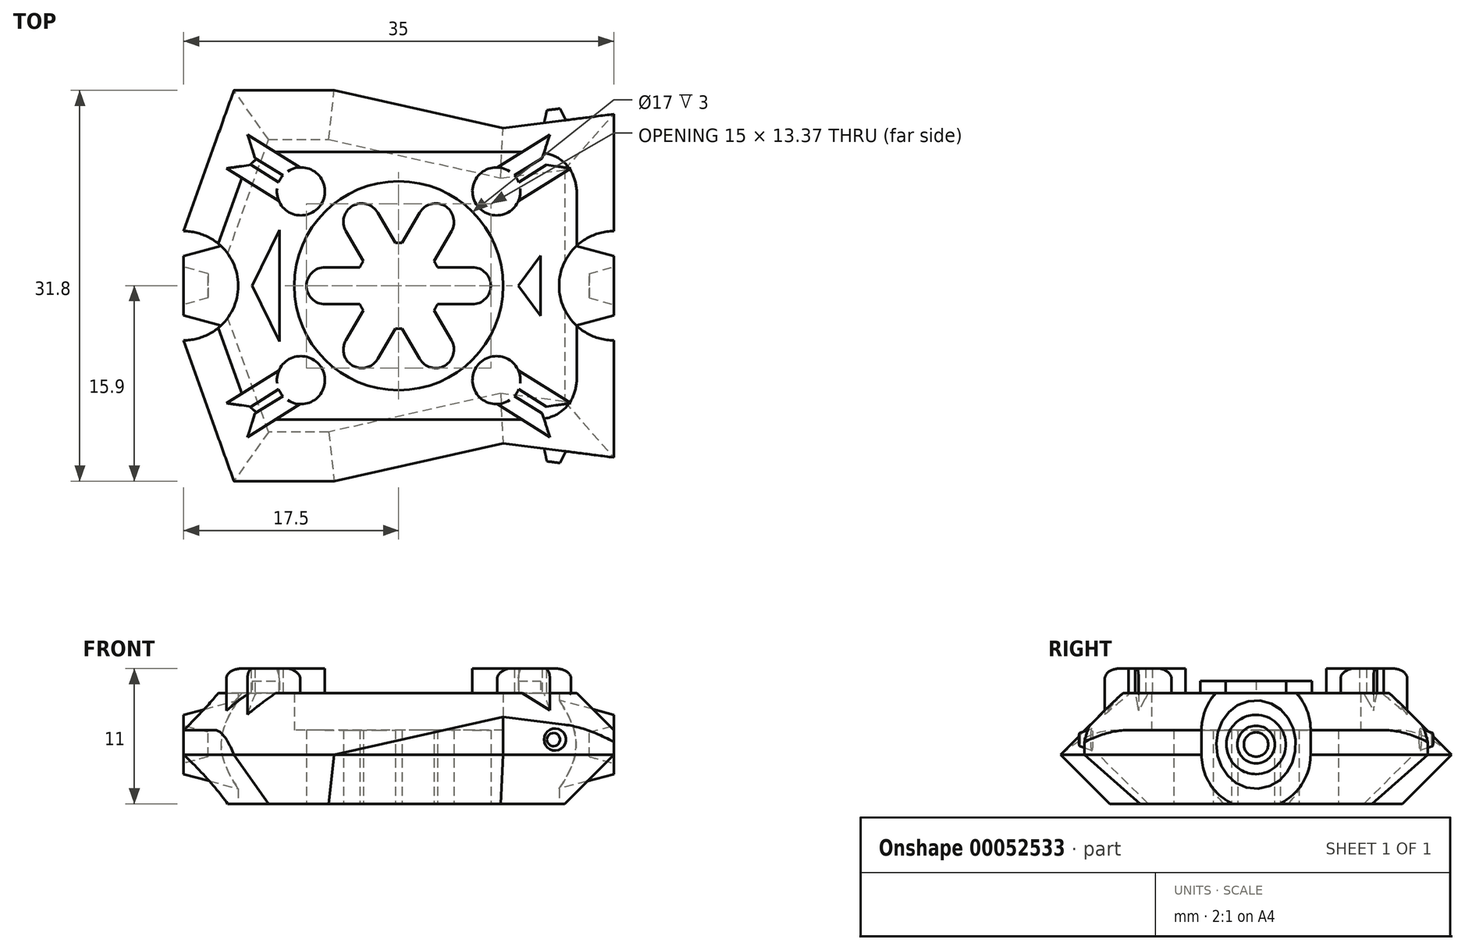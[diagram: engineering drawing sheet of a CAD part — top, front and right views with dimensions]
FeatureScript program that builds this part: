
annotation { "Feature Type Name" : "Feature", "Feature Type Description" : "" }
export const myFeature = defineFeature(function(context is Context, id is Id, definition is map)
    precondition{}
    {
        {
            var Q0;
            Q0=qCreatedBy(makeId("Top.planeOp"),FACE);
            var sketch = newSketch(context, id + "F0", { "sketchPlane" : qUnion([Q0])});
            skCircle(sketch, "E0", {"center": v(0, 0) * mm, "radius": 8.5 * mm});
            skCircle(sketch, "E1", {"center": v(0, 0) * mm, "radius": 3.5 * mm});
            skArc(sketch, "E2", {"start": v(6, -1.5) * mm, "mid": v(7.5, 0) * mm, "end": v(6, 1.5) * mm});
            skLineSegment(sketch, "E3", {"start": v(6, 1.5) * mm, "end": v(0, 1.5) * mm});
            skLineSegment(sketch, "E4", {"start": v(6, -1.5) * mm, "end": v(0, -1.5) * mm});
            skLineSegment(sketch, "E5.1.0", {"start": v(1.7, 5.95) * mm, "end": v(-1.3, 0.75) * mm});
            skLineSegment(sketch, "E5.1.1", {"start": v(4.3, 4.45) * mm, "end": v(1.3, -0.75) * mm});
            skArc(sketch, "E5.1.2", {"start": v(4.3, 4.45) * mm, "mid": v(3.75, 6.5) * mm, "end": v(1.7, 5.95) * mm});
            skLineSegment(sketch, "E5.2.0", {"start": v(-4.3, 4.45) * mm, "end": v(-1.3, -0.75) * mm});
            skLineSegment(sketch, "E5.2.1", {"start": v(-1.7, 5.95) * mm, "end": v(1.3, 0.75) * mm});
            skArc(sketch, "E5.2.2", {"start": v(-1.7, 5.95) * mm, "mid": v(-3.75, 6.5) * mm, "end": v(-4.3, 4.45) * mm});
            skLineSegment(sketch, "E5.3.0", {"start": v(-6, -1.5) * mm, "end": v(0, -1.5) * mm});
            skLineSegment(sketch, "E5.3.1", {"start": v(-6, 1.5) * mm, "end": v(0, 1.5) * mm});
            skArc(sketch, "E5.3.2", {"start": v(-6, 1.5) * mm, "mid": v(-7.5, 0) * mm, "end": v(-6, -1.5) * mm});
            skLineSegment(sketch, "E5.4.0", {"start": v(-1.7, -5.95) * mm, "end": v(1.3, -0.75) * mm});
            skLineSegment(sketch, "E5.4.1", {"start": v(-4.3, -4.45) * mm, "end": v(-1.3, 0.75) * mm});
            skArc(sketch, "E5.4.2", {"start": v(-4.3, -4.45) * mm, "mid": v(-3.75, -6.5) * mm, "end": v(-1.7, -5.95) * mm});
            skLineSegment(sketch, "E5.5.0", {"start": v(4.3, -4.45) * mm, "end": v(1.3, 0.75) * mm});
            skLineSegment(sketch, "E5.5.1", {"start": v(1.7, -5.95) * mm, "end": v(-1.3, -0.75) * mm});
            skArc(sketch, "E5.5.2", {"start": v(1.7, -5.95) * mm, "mid": v(3.75, -6.5) * mm, "end": v(4.3, -4.45) * mm});
            skSolve(sketch);
        }
        {
            var Q0;
            Q0=makeQuery(id+"F0.imprint","IMPRINT",FACE,{"disambiguationData":[TD([[makeQuery(id+"F0.imprint","IMPRINT",EDGE,{"derivedFrom":sQuery(id+"F0.wireOp",EDGE,"E0")}),1.0]])]});
            extrude(context, id + "F1", {"entities" : qUnion([Q0]), "depth" : 6 * mm});
        }
        {
            var Q0;
            Q0=qCreatedBy(makeId("Top.planeOp"),FACE);
            var sketch = newSketch(context, id + "F2", { "sketchPlane" : qUnion([Q0])});
            skCircle(sketch, "E6", {"center": v(0, 0) * mm, "radius": 17.5 * mm, "construction": true});
            skLineSegment(sketch, "E7", {"start": v(0, 0) * mm, "end": v(17.5, 0) * mm, "construction": true});
            skLineSegment(sketch, "E8", {"start": v(17.5, 4.44) * mm, "end": v(17.5, 13.97) * mm});
            skLineSegment(sketch, "E9", {"start": v(17.5, 13.97) * mm, "end": v(8.48, 12.83) * mm});
            skLineSegment(sketch, "E10", {"start": v(8.48, 12.83) * mm, "end": v(-5.25, 15.9) * mm});
            skLineSegment(sketch, "E11", {"start": v(-5.25, 15.9) * mm, "end": v(-13.41, 15.9) * mm});
            skLineSegment(sketch, "E12", {"start": v(-13.41, 15.9) * mm, "end": v(-17.5, 4.44) * mm});
            skLineSegment(sketch, "E13.MirrorCS", {"start": v(17.5, -4.44) * mm, "end": v(17.5, -13.97) * mm});
            skLineSegment(sketch, "E14.MirrorCS", {"start": v(17.5, -13.97) * mm, "end": v(8.48, -12.83) * mm});
            skLineSegment(sketch, "E15.MirrorCS", {"start": v(8.48, -12.83) * mm, "end": v(-5.25, -15.9) * mm});
            skLineSegment(sketch, "E16.MirrorCS", {"start": v(-5.25, -15.9) * mm, "end": v(-13.41, -15.9) * mm});
            skLineSegment(sketch, "E17.MirrorCS", {"start": v(-13.41, -15.9) * mm, "end": v(-17.5, -4.44) * mm});
            skCircle(sketch, "E18.0", {"center": v(0, 0) * mm, "radius": 8.5 * mm});
            skArc(sketch, "E19", {"start": v(-17.5, -4.44) * mm, "mid": v(-13.06, 0) * mm, "end": v(-17.5, 4.44) * mm});
            skArc(sketch, "E20", {"start": v(17.5, 4.44) * mm, "mid": v(13.06, 0) * mm, "end": v(17.5, -4.44) * mm});
            skPoint(sketch, "E21.MirrorCS.start.orphan", {"position": v(-17.5, -4.44) * mm});
            skSolve(sketch);
        }
        {
            var Q0;
            Q0=makeQuery(id+"F2.imprint","IMPRINT",FACE,{"disambiguationData":[TD([[makeQuery(id+"F2.imprint","IMPRINT",EDGE,{"derivedFrom":sQuery(id+"F2.wireOp",EDGE,"4e53f2e0-acf4-4f54-9269-2bd7d46531fc")}),-1.0]])]});
            var Q1;
            Q1=makeQuery(id+"F2.imprint","IMPRINT",FACE,{"disambiguationData":[TD([[makeQuery(id+"F2.imprint","IMPRINT",EDGE,{"derivedFrom":sQuery(id+"F2.wireOp",EDGE,"E8")}),1.0]])]});
            extrude(context, id + "F3", {"entities" : qUnion([Q0, Q1]), "operationType" : NewBodyOperationType.ADD, "depth" : 9 * mm});
        }
        {
            var Q0;
            Q0=makeQuery(id+"F3.opExtrude","CAP_EDGE",EDGE,{"disambiguationData":[OSD([sQuery(id+"F2.wireOp",EDGE,"E13.MirrorCS")])],"isStart":true});
            var Q1;
            Q1=makeQuery(id+"F3.opExtrude","CAP_EDGE",EDGE,{"disambiguationData":[OSD([sQuery(id+"F2.wireOp",EDGE,"E14.MirrorCS")])],"isStart":true});
            var Q2;
            Q2=makeQuery(id+"F3.opExtrude","CAP_EDGE",EDGE,{"disambiguationData":[OSD([sQuery(id+"F2.wireOp",EDGE,"E15.MirrorCS")])],"isStart":true});
            var Q3;
            Q3=makeQuery(id+"F3.opExtrude","CAP_EDGE",EDGE,{"disambiguationData":[OSD([sQuery(id+"F2.wireOp",EDGE,"E16.MirrorCS")])],"isStart":true});
            var Q4;
            Q4=makeQuery(id+"F3.opExtrude","CAP_EDGE",EDGE,{"disambiguationData":[OSD([sQuery(id+"F2.wireOp",EDGE,"E17.MirrorCS")])],"isStart":true});
            var Q5;
            Q5=makeQuery(id+"F3.opExtrude","CAP_EDGE",EDGE,{"disambiguationData":[OSD([sQuery(id+"F2.wireOp",EDGE,"E12")])],"isStart":true});
            var Q6;
            Q6=makeQuery(id+"F3.opExtrude","CAP_EDGE",EDGE,{"disambiguationData":[OSD([sQuery(id+"F2.wireOp",EDGE,"E11")])],"isStart":true});
            var Q7;
            Q7=makeQuery(id+"F3.opExtrude","CAP_EDGE",EDGE,{"disambiguationData":[OSD([sQuery(id+"F2.wireOp",EDGE,"E10")])],"isStart":true});
            var Q8;
            Q8=makeQuery(id+"F3.opExtrude","CAP_EDGE",EDGE,{"disambiguationData":[OSD([sQuery(id+"F2.wireOp",EDGE,"E9")])],"isStart":true});
            var Q9;
            Q9=makeQuery(id+"F3.opExtrude","CAP_EDGE",EDGE,{"disambiguationData":[OSD([sQuery(id+"F2.wireOp",EDGE,"E8")])],"isStart":true});
            chamfer(context, id + "F4", {"entities" : qUnion([Q0, Q1, Q2, Q3, Q4, Q5, Q6, Q7, Q8, Q9]), "width" : 4 * mm, "tangentPropagation" : true});
        }
        {
            var Q0;
            Q0=makeQuery(id+"F3.opExtrude","CAP_EDGE",EDGE,{"disambiguationData":[OSD([sQuery(id+"F2.wireOp",EDGE,"E8")])],"isStart":false});
            var Q1;
            Q1=makeQuery(id+"F3.opExtrude","CAP_EDGE",EDGE,{"disambiguationData":[OSD([sQuery(id+"F2.wireOp",EDGE,"E13.MirrorCS")])],"isStart":false});
            var Q2;
            Q2=makeQuery(id+"F3.opExtrude","CAP_EDGE",EDGE,{"disambiguationData":[OSD([sQuery(id+"F2.wireOp",EDGE,"E12")])],"isStart":false});
            var Q3;
            Q3=makeQuery(id+"F3.opExtrude","CAP_EDGE",EDGE,{"disambiguationData":[OSD([sQuery(id+"F2.wireOp",EDGE,"E17.MirrorCS")])],"isStart":false});
            chamfer(context, id + "F5", {"entities" : qUnion([Q0, Q1, Q2, Q3]), "width" : 3 * mm, "tangentPropagation" : true});
        }
        {
            var Q0;
            Q0=makeQuery(id+"F3.opExtrude","CAP_EDGE",EDGE,{"disambiguationData":[OSD([sQuery(id+"F2.wireOp",EDGE,"E11")])],"isStart":false});
            var Q1;
            Q1=makeQuery(id+"F3.opExtrude","CAP_EDGE",EDGE,{"disambiguationData":[OSD([sQuery(id+"F2.wireOp",EDGE,"E16.MirrorCS")])],"isStart":false});
            chamfer(context, id + "F6", {"entities" : qUnion([Q0, Q1]), "width" : 5 * mm, "tangentPropagation" : true});
        }
        {
            var Q0;
            Q0=makeQuery(id+"F6.opChamfer","BLEND_EDGE",EDGE,{"blendedFrom":[makeQuery(id+"F3.opExtrude","CAP_EDGE",EDGE,{"disambiguationData":[OSD([sQuery(id+"F2.wireOp",EDGE,"E11")])],"isStart":false}),makeQuery(id+"F5.opChamfer","BLEND_FACE",FACE,{"disambiguationData":[OSD([sQuery(id+"F2.wireOp",EDGE,"E12")])]})],"blendedInto":[makeQuery(id+"F5.opChamfer","BLEND_FACE",FACE,{"disambiguationData":[OSD([sQuery(id+"F2.wireOp",EDGE,"E12")])]})]});
            var Q1;
            Q1=makeQuery(id+"F6.opChamfer","BLEND_EDGE",EDGE,{"blendedFrom":[makeQuery(id+"F3.opExtrude","CAP_EDGE",EDGE,{"disambiguationData":[OSD([sQuery(id+"F2.wireOp",EDGE,"E16.MirrorCS")])],"isStart":false}),makeQuery(id+"F5.opChamfer","BLEND_FACE",FACE,{"disambiguationData":[OSD([sQuery(id+"F2.wireOp",EDGE,"E17.MirrorCS")])]})],"blendedInto":[makeQuery(id+"F5.opChamfer","BLEND_FACE",FACE,{"disambiguationData":[OSD([sQuery(id+"F2.wireOp",EDGE,"E17.MirrorCS")])]})]});
            var Q2;
            Q2=makeQuery(id+"F6.opChamfer","BLEND_EDGE",EDGE,{"blendedFrom":[makeQuery(id+"F3.opExtrude","CAP_EDGE",EDGE,{"disambiguationData":[OSD([sQuery(id+"F2.wireOp",EDGE,"E16.MirrorCS")])],"isStart":false}),makeQuery(id+"F5.opChamfer","BLEND_FACE",FACE,{"disambiguationData":[OSD([sQuery(id+"F2.wireOp",EDGE,"E13.MirrorCS")])]})],"blendedInto":[makeQuery(id+"F5.opChamfer","BLEND_FACE",FACE,{"disambiguationData":[OSD([sQuery(id+"F2.wireOp",EDGE,"E13.MirrorCS")])]})]});
            var Q3;
            Q3=makeQuery(id+"F6.opChamfer","BLEND_EDGE",EDGE,{"blendedFrom":[makeQuery(id+"F3.opExtrude","CAP_EDGE",EDGE,{"disambiguationData":[OSD([sQuery(id+"F2.wireOp",EDGE,"E11")])],"isStart":false}),makeQuery(id+"F5.opChamfer","BLEND_FACE",FACE,{"disambiguationData":[OSD([sQuery(id+"F2.wireOp",EDGE,"E8")])]})],"blendedInto":[makeQuery(id+"F5.opChamfer","BLEND_FACE",FACE,{"disambiguationData":[OSD([sQuery(id+"F2.wireOp",EDGE,"E8")])]})]});
            fillet(context, id + "F7", {"entities" : qUnion([Q0, Q1, Q2, Q3]), "radius" : 5 * mm, "tangentPropagation" : true, "allowEdgeOverflow" : false});
        }
        {
            var Q0;
            Q0=makeQuery(id+"F3.opExtrude","SWEPT_FACE",FACE,{"disambiguationData":[OSD([sQuery(id+"F2.wireOp",EDGE,"E9")])]});
            var sketch = newSketch(context, id + "F8", { "sketchPlane" : qUnion([Q0])});
            skCircle(sketch, "E22", {"center": v(-14.3, 5.22) * mm, "radius": 0.9 * mm});
            skSolve(sketch);
        }
        {
            var Q0;
            Q0=makeQuery(id+"F8.imprint","IMPRINT",FACE,{"disambiguationData":[TD([[makeQuery(id+"F8.imprint","IMPRINT",EDGE,{"derivedFrom":sQuery(id+"F8.wireOp",EDGE,"E22")}),1.0]])]});
            extrude(context, id + "F9", {"entities" : qUnion([Q0]), "depth" : 1 * mm, "hasDraft" : true, "draftAngle" : 20 * degree, "draftPullDirection" : true});
        }
        {
            var Q0;
            Q0=makeQuery(id+"F3.opExtrude","CAP_FACE",FACE,{"disambiguationData":[OSD([sQuery(id+"F2.wireOp",EDGE,"E8"),sQuery(id+"F2.wireOp",EDGE,"E9"),sQuery(id+"F2.wireOp",EDGE,"E10"),sQuery(id+"F2.wireOp",EDGE,"E11"),sQuery(id+"F2.wireOp",EDGE,"E12"),sQuery(id+"F2.wireOp",EDGE,"E13.MirrorCS"),sQuery(id+"F2.wireOp",EDGE,"E14.MirrorCS"),sQuery(id+"F2.wireOp",EDGE,"E15.MirrorCS"),sQuery(id+"F2.wireOp",EDGE,"E16.MirrorCS"),sQuery(id+"F2.wireOp",EDGE,"E17.MirrorCS"),sQuery(id+"F2.wireOp",EDGE,"E18.0"),sQuery(id+"F2.wireOp",EDGE,"E19"),sQuery(id+"F2.wireOp",EDGE,"E20")])],"isStart":false});
            var sketch = newSketch(context, id + "F10", { "sketchPlane" : qUnion([Q0])});
            skCircle(sketch, "E23", {"center": v(7.96, 7.68) * mm, "radius": 1.95 * mm});
            skLineSegment(sketch, "E24", {"start": v(7.96, 7.68) * mm, "end": v(13.91, 11.4) * mm, "construction": true});
            skLineSegment(sketch, "E25", {"start": v(9.76, 8.43) * mm, "end": v(12.03, 9.84) * mm});
            skLineSegment(sketch, "E26", {"start": v(12.03, 9.84) * mm, "end": v(14.02, 9.55) * mm});
            skLineSegment(sketch, "E27", {"start": v(14.02, 9.55) * mm, "end": v(9.74, 6.88) * mm});
            skLineSegment(sketch, "E28.MirrorCS", {"start": v(9.42, 8.98) * mm, "end": v(11.68, 10.39) * mm});
            skLineSegment(sketch, "E29.MirrorCS", {"start": v(12.3, 12.3) * mm, "end": v(8.02, 9.63) * mm});
            skLineSegment(sketch, "E30.MirrorCS", {"start": v(11.68, 10.39) * mm, "end": v(12.3, 12.3) * mm});
            skLineSegment(sketch, "E31", {"start": v(0, 0) * mm, "end": v(0, 17.3) * mm, "construction": true});
            skCircle(sketch, "E32.MirrorC", {"center": v(-7.96, 7.68) * mm, "radius": 1.95 * mm});
            skLineSegment(sketch, "E33.MirrorCS", {"start": v(-12.3, 12.3) * mm, "end": v(-8.02, 9.63) * mm});
            skLineSegment(sketch, "E34.MirrorCS", {"start": v(-11.68, 10.39) * mm, "end": v(-12.3, 12.3) * mm});
            skLineSegment(sketch, "E35.MirrorCS", {"start": v(-9.42, 8.98) * mm, "end": v(-11.68, 10.39) * mm});
            skLineSegment(sketch, "E36.MirrorCS", {"start": v(-9.76, 8.43) * mm, "end": v(-12.03, 9.84) * mm});
            skLineSegment(sketch, "E37.MirrorCS", {"start": v(-12.03, 9.84) * mm, "end": v(-14.02, 9.55) * mm});
            skLineSegment(sketch, "E38.MirrorCS", {"start": v(-14.02, 9.55) * mm, "end": v(-9.74, 6.88) * mm});
            skLineSegment(sketch, "E39", {"start": v(-9.19, 4.5) * mm, "end": v(-11.11, 3.53) * mm});
            skPoint(sketch, "E39.endSnap0", {"position": v(-11.11, 0.95) * mm});
            skLineSegment(sketch, "E40", {"start": v(-11.11, 3.53) * mm, "end": v(-12.2, 0.77) * mm});
            skLineSegment(sketch, "E41", {"start": v(-12.2, 0.77) * mm, "end": v(-9.19, 4.5) * mm});
            skSolve(sketch);
        }
        {
            var Q0;
            {var subQ0=sQuery(id+"F10.wireOp",EDGE,"E23");var subQ1=makeQuery(id+"F10.imprint","INTERSECT",VERTEX,{"derivedFrom":[subQ0,sQuery(id+"F10.wireOp",EDGE,"E25")]});Q0=makeQuery(id+"F10.imprint","IMPRINT",FACE,{"disambiguationData":[TD([[makeQuery(id+"F10.imprint","IMPRINT",EDGE,{"disambiguationData":[TD([[subQ1,-1.0]])],"derivedFrom":subQ0}),1.0]])]});}
            var Q1;
            {var subQ8=sQuery(id+"F10.wireOp",EDGE,"E25");Q1=makeQuery(id+"F10.imprint","IMPRINT",FACE,{"disambiguationData":[TD([[makeQuery(id+"F10.imprint","IMPRINT",EDGE,{"derivedFrom":subQ8}),-1.0]])]});}
            var Q2;
            {var subQ10=sQuery(id+"F10.wireOp",EDGE,"E28.MirrorCS");Q2=makeQuery(id+"F10.imprint","IMPRINT",FACE,{"disambiguationData":[TD([[makeQuery(id+"F10.imprint","IMPRINT",EDGE,{"derivedFrom":subQ10}),1.0]])]});}
            var Q3;
            {var subQ0=sQuery(id+"F10.wireOp",EDGE,"E30.MirrorCS");var subQ1=sQuery(id+"F10.wireOp",EDGE,"E29.MirrorCS");var subQ2=makeQuery(id+"F10.imprint","INTERSECT",VERTEX,{"derivedFrom":[subQ1,subQ0]});Q3=makeQuery(id+"F10.imprint","IMPRINT",FACE,{"disambiguationData":[TD([[makeQuery(id+"F10.imprint","IMPRINT",EDGE,{"disambiguationData":[TD([[subQ2,-1.0]])],"derivedFrom":subQ1}),1.0]])]});}
            var Q4;
            {var subQ0=sQuery(id+"F10.wireOp",EDGE,"E27");var subQ1=sQuery(id+"F10.wireOp",EDGE,"E26");var subQ2=makeQuery(id+"F10.imprint","INTERSECT",VERTEX,{"derivedFrom":[subQ1,subQ0]});Q4=makeQuery(id+"F10.imprint","IMPRINT",FACE,{"disambiguationData":[TD([[makeQuery(id+"F10.imprint","IMPRINT",EDGE,{"disambiguationData":[TD([[subQ2,1.0]])],"derivedFrom":subQ1}),-1.0]])]});}
            var Q5;
            {var subQ0=sQuery(id+"F10.wireOp",EDGE,"E32.MirrorC");var subQ1=makeQuery(id+"F10.imprint","INTERSECT",VERTEX,{"derivedFrom":[subQ0,sQuery(id+"F10.wireOp",EDGE,"E35.MirrorCS")]});Q5=makeQuery(id+"F10.imprint","IMPRINT",FACE,{"disambiguationData":[TD([[makeQuery(id+"F10.imprint","IMPRINT",EDGE,{"disambiguationData":[TD([[subQ1,1.0]])],"derivedFrom":subQ0}),-1.0]])]});}
            var Q6;
            {var subQ0=sQuery(id+"F10.wireOp",EDGE,"E33.MirrorCS");var subQ1=sQuery(id+"F10.wireOp",EDGE,"E32.MirrorC");var subQ2=makeQuery(id+"F10.imprint","INTERSECT",VERTEX,{"derivedFrom":[subQ1,subQ0]});Q6=makeQuery(id+"F10.imprint","IMPRINT",FACE,{"disambiguationData":[TD([[makeQuery(id+"F10.imprint","IMPRINT",EDGE,{"disambiguationData":[TD([[subQ2,1.0]])],"derivedFrom":subQ1}),1.0]])]});}
            var Q7;
            {var subQ0=sQuery(id+"F10.wireOp",EDGE,"E34.MirrorCS");Q7=makeQuery(id+"F10.imprint","IMPRINT",FACE,{"disambiguationData":[TD([[makeQuery(id+"F10.imprint","IMPRINT",EDGE,{"derivedFrom":subQ0}),-1.0]])]});}
            var Q8;
            {var subQ0=sQuery(id+"F10.wireOp",EDGE,"E38.MirrorCS");var subQ1=sQuery(id+"F10.wireOp",EDGE,"E37.MirrorCS");var subQ2=makeQuery(id+"F10.imprint","INTERSECT",VERTEX,{"derivedFrom":[subQ1,subQ0]});Q8=makeQuery(id+"F10.imprint","IMPRINT",FACE,{"disambiguationData":[TD([[makeQuery(id+"F10.imprint","IMPRINT",EDGE,{"disambiguationData":[TD([[subQ2,1.0]])],"derivedFrom":subQ1}),1.0]])]});}
            var Q9;
            {var subQ8=sQuery(id+"F10.wireOp",EDGE,"E36.MirrorCS");Q9=makeQuery(id+"F10.imprint","IMPRINT",FACE,{"disambiguationData":[TD([[makeQuery(id+"F10.imprint","IMPRINT",EDGE,{"derivedFrom":subQ8}),1.0]])]});}
            extrude(context, id + "F11", {"entities" : qUnion([Q0, Q1, Q2, Q3, Q4, Q5, Q6, Q7, Q8, Q9]), "depth" : 2 * mm, "hasSecondDirection" : true, "secondDirectionOppositeDirection" : true, "secondDirectionDepth" : 4 * mm});
        }
        {
            var Q0;
            Q0=makeQuery(id+"F11.opExtrude","CAP_EDGE",EDGE,{"disambiguationData":[OSD([sQuery(id+"F10.wireOp",EDGE,"E33.MirrorCS")])],"isStart":false});
            var Q1;
            Q1=makeQuery(id+"F11.opExtrude","CAP_EDGE",EDGE,{"disambiguationData":[OSD([sQuery(id+"F10.wireOp",EDGE,"E38.MirrorCS")])],"isStart":false});
            var Q2;
            Q2=makeQuery(id+"F11.opExtrude","CAP_EDGE",EDGE,{"disambiguationData":[OSD([sQuery(id+"F10.wireOp",EDGE,"E29.MirrorCS")])],"isStart":false});
            var Q3;
            Q3=makeQuery(id+"F11.opExtrude","CAP_EDGE",EDGE,{"disambiguationData":[OSD([sQuery(id+"F10.wireOp",EDGE,"E27")])],"isStart":false});
            fillet(context, id + "F12", {"entities" : qUnion([Q0, Q1, Q2, Q3]), "radius" : 0.8 * mm, "tangentPropagation" : true, "allowEdgeOverflow" : false});
        }
        {
            var Q0;
            Q0=makeQuery(id+"F3.opExtrude","SWEPT_FACE",FACE,{"disambiguationData":[OSD([sQuery(id+"F2.wireOp",EDGE,"E8")])]});
            var sketch = newSketch(context, id + "F13", { "sketchPlane" : qUnion([Q0])});
            skCircle(sketch, "E42", {"center": v(0, 4.82) * mm, "radius": 2.41 * mm});
            skSolve(sketch);
        }
        {
            var Q0;
            Q0=makeQuery(id+"F13.imprint","IMPRINT",FACE,{"disambiguationData":[TD([[makeQuery(id+"F13.imprint","IMPRINT",EDGE,{"derivedFrom":sQuery(id+"F13.wireOp",EDGE,"E42")}),1.0]])]});
            extrude(context, id + "F14", {"entities" : qUnion([Q0]), "endBound" : BoundingType.UP_TO_NEXT, "oppositeDirection" : true, "depth" : 25 * mm, "hasDraft" : true, "draftAngle" : 15 * degree});
        }
        {
            var Q0;
            Q0=makeQuery(id+"F14.opExtrude","CAP_FACE",FACE,{"disambiguationData":[OSD([sQuery(id+"F13.wireOp",EDGE,"E42")])],"isStart":true});
            var sketch = newSketch(context, id + "F15", { "sketchPlane" : qUnion([Q0])});
            skCircle(sketch, "E43", {"center": v(0, 4.82) * mm, "radius": 1.53 * mm});
            skSolve(sketch);
        }
        {
            var Q0;
            Q0=makeQuery(id+"F15.imprint","IMPRINT",FACE,{"disambiguationData":[TD([[makeQuery(id+"F15.imprint","IMPRINT",EDGE,{"derivedFrom":sQuery(id+"F15.wireOp",EDGE,"E43")}),1.0]])]});
            extrude(context, id + "F16", {"entities" : qUnion([Q0]), "operationType" : NewBodyOperationType.REMOVE, "oppositeDirection" : true, "depth" : 2 * mm, "hasDraft" : true, "draftAngle" : 15 * degree, "draftPullDirection" : true});
        }
        {
            var Q0;
            Q0=makeQuery(id+"F3.opExtrude","CAP_FACE",FACE,{"disambiguationData":[OSD([sQuery(id+"F2.wireOp",EDGE,"E8"),sQuery(id+"F2.wireOp",EDGE,"E9"),sQuery(id+"F2.wireOp",EDGE,"E10"),sQuery(id+"F2.wireOp",EDGE,"E11"),sQuery(id+"F2.wireOp",EDGE,"E12"),sQuery(id+"F2.wireOp",EDGE,"E13.MirrorCS"),sQuery(id+"F2.wireOp",EDGE,"E14.MirrorCS"),sQuery(id+"F2.wireOp",EDGE,"E15.MirrorCS"),sQuery(id+"F2.wireOp",EDGE,"E16.MirrorCS"),sQuery(id+"F2.wireOp",EDGE,"E17.MirrorCS"),sQuery(id+"F2.wireOp",EDGE,"E18.0"),sQuery(id+"F2.wireOp",EDGE,"E19"),sQuery(id+"F2.wireOp",EDGE,"E20")])],"isStart":false});
            var sketch = newSketch(context, id + "F17", { "sketchPlane" : qUnion([Q0])});
            skLineSegment(sketch, "E44", {"start": v(-11.92, 0) * mm, "end": v(-9.7, 4.53) * mm});
            skLineSegment(sketch, "E45", {"start": v(9.74, 0) * mm, "end": v(11.56, 2.46) * mm});
            skLineSegment(sketch, "E46", {"start": v(0, 0) * mm, "end": v(-26.9, 0) * mm, "construction": true});
            skPoint(sketch, "E47", {"position": v(-13.06, 0) * mm});
            skLineSegment(sketch, "E48.MirrorCS", {"start": v(-11.92, 0) * mm, "end": v(-9.7, -4.53) * mm});
            skLineSegment(sketch, "E49.MirrorCS", {"start": v(9.74, 0) * mm, "end": v(11.56, -2.46) * mm});
            skLineSegment(sketch, "E50", {"start": v(-9.7, 4.53) * mm, "end": v(-9.7, -4.53) * mm});
            skLineSegment(sketch, "E51", {"start": v(11.56, 2.46) * mm, "end": v(11.56, -2.46) * mm});
            skSolve(sketch);
        }
        {
            var Q0;
            Q0=makeQuery(id+"F17.imprint","IMPRINT",FACE,{"disambiguationData":[TD([[makeQuery(id+"F17.imprint","IMPRINT",EDGE,{"derivedFrom":sQuery(id+"F17.wireOp",EDGE,"E44")}),-1.0]])]});
            var Q1;
            Q1=makeQuery(id+"F17.imprint","IMPRINT",FACE,{"disambiguationData":[TD([[makeQuery(id+"F17.imprint","IMPRINT",EDGE,{"derivedFrom":sQuery(id+"F17.wireOp",EDGE,"E45")}),-1.0]])]});
            extrude(context, id + "F18", {"entities" : qUnion([Q0, Q1]), "operationType" : NewBodyOperationType.ADD, "depth" : 1 * mm});
        }
        {
            var Q0;
            Q0=makeQuery(id+"F9.opExtrude","SWEPT_BODY",BODY,{"disambiguationData":[OSD([sQuery(id+"F8.wireOp",EDGE,"E22")])]});
            var Q1;
            Q1=makeQuery(id+"F11.opExtrude","SWEPT_BODY",BODY,{"disambiguationData":[OSD([sQuery(id+"F10.wireOp",EDGE,"E23"),sQuery(id+"F10.wireOp",EDGE,"E25"),sQuery(id+"F10.wireOp",EDGE,"E26"),sQuery(id+"F10.wireOp",EDGE,"E27"),sQuery(id+"F10.wireOp",EDGE,"E28.MirrorCS"),sQuery(id+"F10.wireOp",EDGE,"E29.MirrorCS"),sQuery(id+"F10.wireOp",EDGE,"E30.MirrorCS")])]});
            var Q2;
            Q2=makeQuery(id+"F11.opExtrude","SWEPT_BODY",BODY,{"disambiguationData":[OSD([sQuery(id+"F10.wireOp",EDGE,"E32.MirrorC"),sQuery(id+"F10.wireOp",EDGE,"E33.MirrorCS"),sQuery(id+"F10.wireOp",EDGE,"E34.MirrorCS"),sQuery(id+"F10.wireOp",EDGE,"E35.MirrorCS"),sQuery(id+"F10.wireOp",EDGE,"E36.MirrorCS"),sQuery(id+"F10.wireOp",EDGE,"E37.MirrorCS"),sQuery(id+"F10.wireOp",EDGE,"E38.MirrorCS")])]});
            var Q3;
            Q3=qCreatedBy(makeId("Front.planeOp"),FACE);
            mirror(context, id + "F19", {"operationType" : NewBodyOperationType.ADD, "entities" : qUnion([Q0, Q1, Q2]), "mirrorPlane" : qUnion([Q3])});
        }
        {
            var Q0;
            Q0=makeQuery(id+"F14.opExtrude","SWEPT_BODY",BODY,{"disambiguationData":[OSD([sQuery(id+"F13.wireOp",EDGE,"E42")])]});
            var Q1;
            Q1=qCreatedBy(makeId("Right.planeOp"),FACE);
            mirror(context, id + "F20", {"operationType" : NewBodyOperationType.ADD, "entities" : qUnion([Q0]), "mirrorPlane" : qUnion([Q1])});
        }
    });
